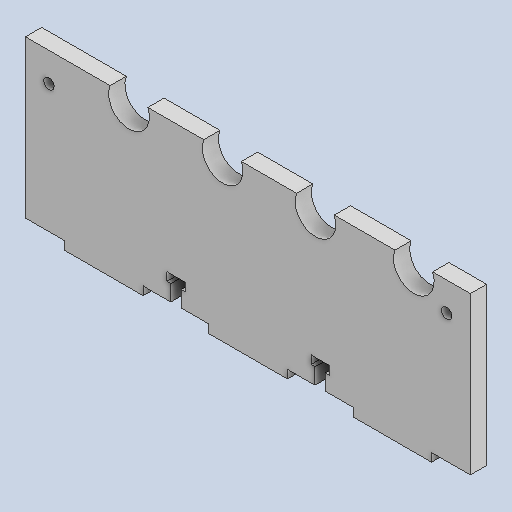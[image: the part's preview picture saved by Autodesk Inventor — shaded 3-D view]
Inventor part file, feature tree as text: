
AUTODESK INVENTOR PART (.ipt)
format: ipt  version: 2022 (Build 260153000, 153)  size: 196,096 bytes
history: native  units: mm
features: reference x16, other x7, extrude x2, sketch x2
ambient origin geometry x8: Origin, YZ Plane, XZ Plane, XY Plane, X Axis, Y Axis, Z Axis, Center Point
bodies: Body1 (feature_tree)
feature tree (27):
  extrude  "Extrusion3"  Depth=170.0mm
  extrude  "Extrusion4"  Depth=7.0mm
  sketch  "Sketch1"  dims[d2=170.0mm d4=0.3mm]
  reference  "Reference1"
  reference  "Reference2"
  reference  "Reference3"
  reference  "Reference4"
  reference  "Reference5"
  reference  "Reference6"
  reference  "Reference7"
  reference  "Reference8"
  reference  "Reference9"
  reference  "Reference10"
  reference  "Reference11"
  reference  "Reference12"
  reference  "Reference13"
  reference  "Reference14"
  reference  "Reference15"
  reference  "Reference16"
  sketch  "Sketch2"  dims[d5=0.3mm d6=0.3mm d7=0.3mm d17=4.0mm d19=8.0mm d24=9.0mm d42=60.0mm d43=30.0mm d44=3.2mm d45=15.0mm d46=75.186774mm d47=94.813226mm d48=9.0mm d49=8.0mm d50=4.0mm d51=3.2mm d52=15.0mm d53=25.093387mm d54=0.1mm d55=6.1mm d56=0.0mm d57=0.0mm d64=2.0mm d65=3.5mm d66=3.2mm d67=4.0mm d68=6.1mm d69=7.0mm d70=7.0mm d71=0.0mm d72=0.5mm d73=0.872665mm]
  other  "Caja_Reductora.iam"
  other  "Rodamiento_Ejes:1"
  other  "Rodamiento_Ejes:2"
  other  "Engranajes_1_5:1"
  other  "Engranajes_1_4:1"
  other  "Rodamiento_Ejes:8"
  other  "Rodamiento_Ejes:7"
